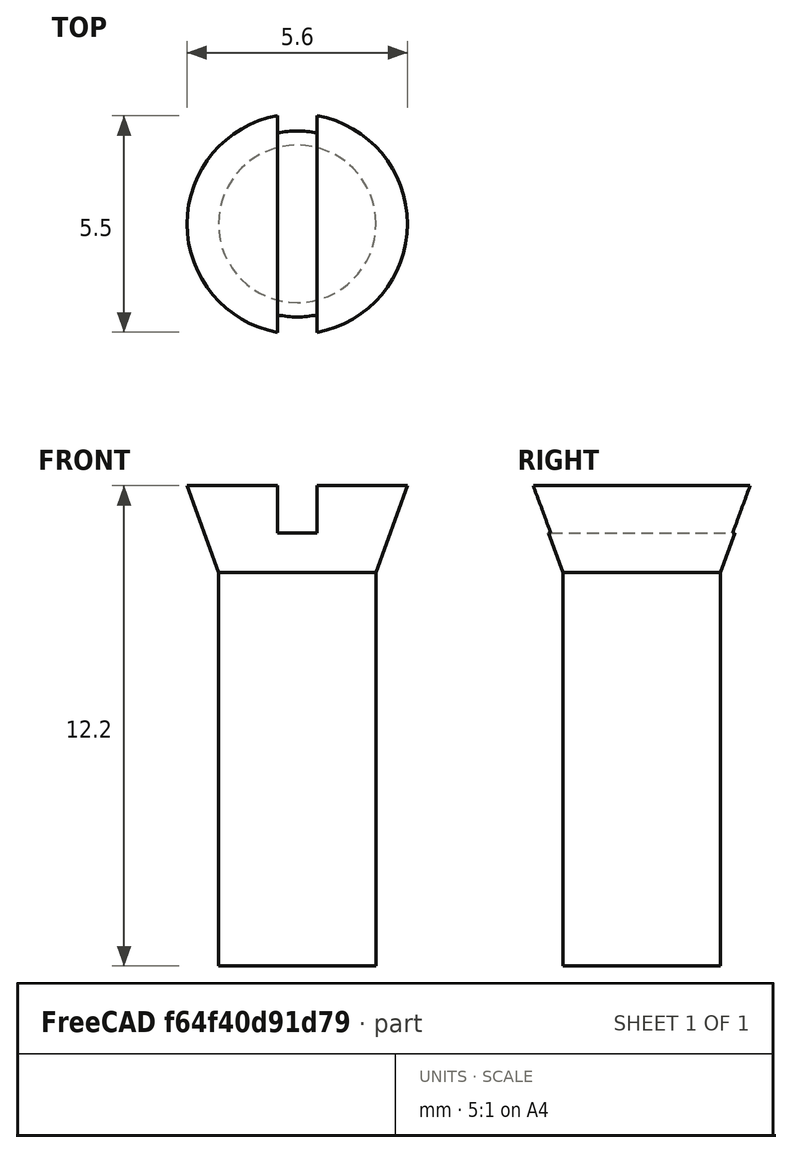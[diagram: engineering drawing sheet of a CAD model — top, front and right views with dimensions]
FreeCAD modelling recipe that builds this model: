
FCSTD DOCUMENT  (FreeCAD 0.21R33694 (Git))
Label: OJT1_T014_cargol
License: All rights reserved
LicenseURL: https://en.wikipedia.org/wiki/All_rights_reserved
objects: Part::Cone×1, Part::Cylinder×1, Part::Box×1, Part::MultiFuse×1, Part::Cut×1
note: 5 computed .brp shape members not serialized (recipe doc carries the construction recipe); baked Part::Feature solids carry a one-line shape summary decoded from their .brp

FEATURE [Part::Cone] Cone  label="Con"
  Angle = 360
  AttacherType = Attacher::AttachEngine3D
  Height = 2.2
  Radius1 = 2
  Radius2 = 2.8
FEATURE [Part::Cylinder] Cylinder  label="Cilindre"
  Angle = 360
  AttacherType = Attacher::AttachEngine3D
  FirstAngle = 0
  Height = 10
  Placement = pos=(0,0,-10) rot=(0,0,1;0rad)
  Radius = 2
  SecondAngle = 0
FEATURE [Part::Box] Box  label="Cub"
  AttacherType = Attacher::AttachEngine3D
  Height = 2
  Length = 1
  Placement = pos=(-0.5,-5,1) rot=(0,0,1;0rad)
  Width = 10
  expr: .Placement.Base.x = -0.5
  expr: .Placement.Base.y = -5
FEATURE [Part::MultiFuse] Fusion
  Shapes = -> [Cone,Cylinder]
FEATURE [Part::Cut] Cut
  Base = -> Fusion
  Tool = -> Box
